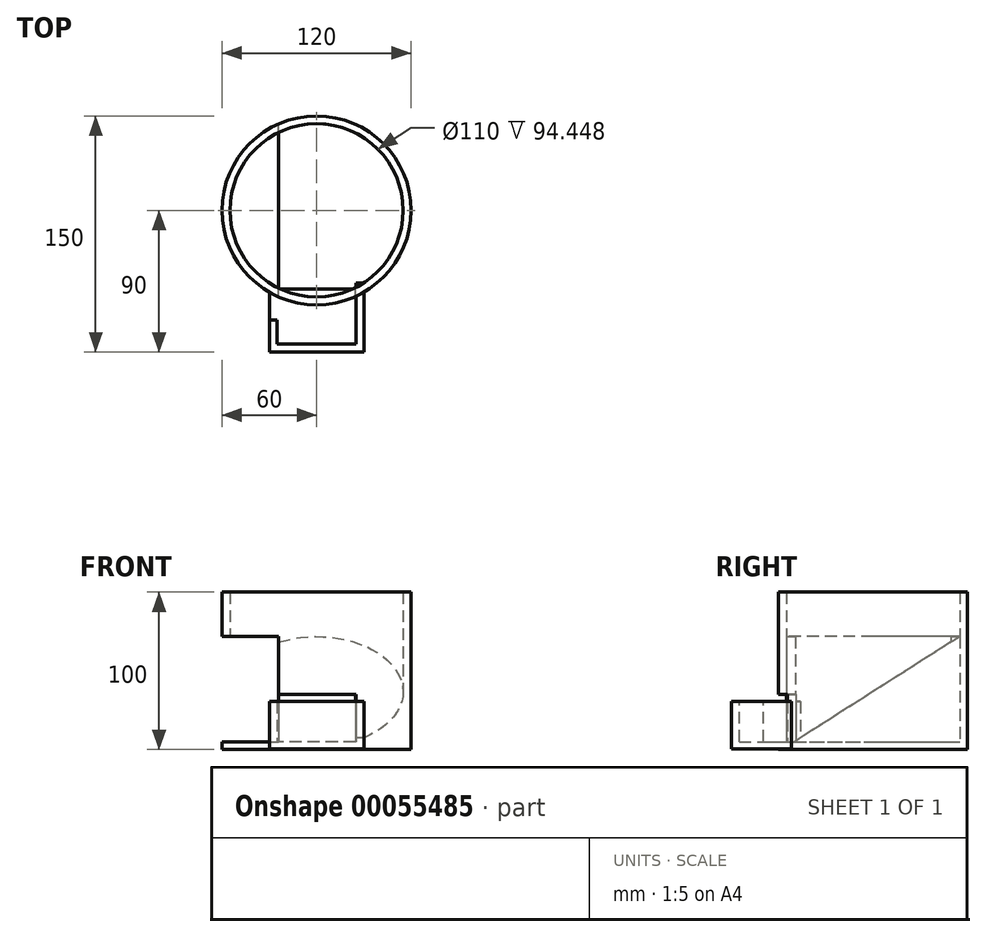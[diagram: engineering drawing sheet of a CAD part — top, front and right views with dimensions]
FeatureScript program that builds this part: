
annotation { "Feature Type Name" : "Feature", "Feature Type Description" : "" }
export const myFeature = defineFeature(function(context is Context, id is Id, definition is map)
    precondition{}
    {
        {
            var Q0;
            Q0=qCreatedBy(makeId("Front.planeOp"),FACE);
            var sketch = newSketch(context, id + "F0", { "sketchPlane" : qUnion([Q0])});
            skLineSegment(sketch, "E0", {"start": v(0, 0) * mm, "end": v(-55, 0) * mm});
            skLineSegment(sketch, "E1", {"start": v(-55, 0) * mm, "end": v(-55, 95) * mm});
            skLineSegment(sketch, "E2", {"start": v(-55, 95) * mm, "end": v(-60, 95) * mm});
            skLineSegment(sketch, "E3", {"start": v(-60, 95) * mm, "end": v(-60, -5) * mm});
            skLineSegment(sketch, "E4", {"start": v(-60, -5) * mm, "end": v(0, -5) * mm});
            skLineSegment(sketch, "E5", {"start": v(0, -5) * mm, "end": v(0, 0) * mm});
            skSolve(sketch);
        }
        {
            var Q0;
            Q0=makeQuery(id+"F0.imprint","IMPRINT",FACE,{"disambiguationData":[TD([[makeQuery(id+"F0.imprint","IMPRINT",EDGE,{"derivedFrom":sQuery(id+"F0.wireOp",EDGE,"E0")}),1.0]])]});
            var Q1;
            Q1=sQuery(id+"F0.wireOp",EDGE,"E5");
            revolve(context, id + "F1", {"entities" : qUnion([Q0]), "axis" : qUnion([Q1]), "revolveType" : RevolveType.FULL});
        }
        {
            var Q0;
            Q0=qCreatedBy(makeId("Front.planeOp"),FACE);
            var sketch = newSketch(context, id + "F2", { "sketchPlane" : qUnion([Q0])});
            skLineSegment(sketch, "E6", {"start": v(0, 0) * mm, "end": v(-26.4, 0) * mm});
            skLineSegment(sketch, "E7", {"start": v(-26.4, 0) * mm, "end": v(-26.4, 30) * mm});
            skLineSegment(sketch, "E8", {"start": v(-26.4, 30) * mm, "end": v(23.6, 30) * mm});
            skLineSegment(sketch, "E9", {"start": v(23.6, 30) * mm, "end": v(23.6, 0) * mm});
            skLineSegment(sketch, "E10", {"start": v(23.6, 0) * mm, "end": v(0, 0) * mm});
            skSolve(sketch);
        }
        {
            var Q0;
            Q0 = qSketchRegion(id + "F2", true);
            extrude(context, id + "F3", {"entities" : qUnion([Q0]), "operationType" : NewBodyOperationType.REMOVE, "depth" : 90 * mm});
        }
        {
            var Q0;
            Q0=qCreatedBy(makeId("Right.planeOp"),FACE);
            var sketch = newSketch(context, id + "F4", { "sketchPlane" : qUnion([Q0])});
            skLineSegment(sketch, "E11", {"start": v(0, 0) * mm, "end": v(0, -4.5) * mm});
            skLineSegment(sketch, "E12", {"start": v(0, -4.5) * mm, "end": v(-90, -4.5) * mm});
            skLineSegment(sketch, "E13", {"start": v(-90, -4.5) * mm, "end": v(-90, 25.5) * mm});
            skLineSegment(sketch, "E14", {"start": v(-90, 25.5) * mm, "end": v(-85, 25.5) * mm});
            skLineSegment(sketch, "E15", {"start": v(-85, 25.5) * mm, "end": v(-85, 0) * mm});
            skLineSegment(sketch, "E16", {"start": v(-85, 0) * mm, "end": v(0, 0) * mm});
            skSolve(sketch);
        }
        {
            var Q0;
            Q0=makeQuery(id+"F4.imprint","IMPRINT",FACE,{"disambiguationData":[TD([[makeQuery(id+"F4.imprint","IMPRINT",EDGE,{"derivedFrom":sQuery(id+"F4.wireOp",EDGE,"E11")}),-1.0]])]});
            extrude(context, id + "F5", {"entities" : qUnion([Q0]), "operationType" : NewBodyOperationType.ADD, "depth" : 25 * mm});
        }
        {
            var Q0;
            Q0=makeQuery(id+"F5.opExtrude","CAP_FACE",FACE,{"disambiguationData":[OSD([sQuery(id+"F4.wireOp",EDGE,"E11"),sQuery(id+"F4.wireOp",EDGE,"E12"),sQuery(id+"F4.wireOp",EDGE,"E13"),sQuery(id+"F4.wireOp",EDGE,"E14"),sQuery(id+"F4.wireOp",EDGE,"E15"),sQuery(id+"F4.wireOp",EDGE,"E16")])],"isStart":true});
            extrude(context, id + "F6", {"entities" : qUnion([Q0]), "operationType" : NewBodyOperationType.ADD, "depth" : 25 * mm});
        }
        {
            var Q0;
            Q0=makeQuery(id+"F5.opExtrude","CAP_FACE",FACE,{"disambiguationData":[OSD([sQuery(id+"F4.wireOp",EDGE,"E11"),sQuery(id+"F4.wireOp",EDGE,"E12"),sQuery(id+"F4.wireOp",EDGE,"E13"),sQuery(id+"F4.wireOp",EDGE,"E14"),sQuery(id+"F4.wireOp",EDGE,"E15"),sQuery(id+"F4.wireOp",EDGE,"E16")])],"isStart":false});
            var sketch = newSketch(context, id + "F7", { "sketchPlane" : qUnion([Q0])});
            skLineSegment(sketch, "E17", {"start": v(-90, 25.5) * mm, "end": v(-85, 25.5) * mm});
            skLineSegment(sketch, "E18", {"start": v(-85, 25.5) * mm, "end": v(-85, -4.5) * mm});
            skLineSegment(sketch, "E19", {"start": v(-85, -4.5) * mm, "end": v(-90, -4.5) * mm});
            skLineSegment(sketch, "E20", {"start": v(-90, -4.5) * mm, "end": v(-90, 25.5) * mm});
            skSolve(sketch);
        }
        {
            var Q0;
            {var subQ2=sQuery(id+"F7.wireOp",EDGE,"E17");Q0=makeQuery(id+"F7.imprint","IMPRINT",FACE,{"disambiguationData":[TD([[makeQuery(id+"F7.imprint","IMPRINT",EDGE,{"derivedFrom":subQ2}),-1.0]])]});}
            extrude(context, id + "F8", {"entities" : qUnion([Q0]), "operationType" : NewBodyOperationType.ADD, "depth" : 5 * mm});
        }
        {
            var Q0;
            Q0=makeQuery(id+"F6.opExtrude","CAP_FACE",FACE,{"disambiguationData":[OSD([sQuery(id+"F4.wireOp",EDGE,"E11"),sQuery(id+"F4.wireOp",EDGE,"E12"),sQuery(id+"F4.wireOp",EDGE,"E13"),sQuery(id+"F4.wireOp",EDGE,"E14"),sQuery(id+"F4.wireOp",EDGE,"E15"),sQuery(id+"F4.wireOp",EDGE,"E16")])],"isStart":false});
            var sketch = newSketch(context, id + "F9", { "sketchPlane" : qUnion([Q0])});
            skLineSegment(sketch, "E21", {"start": v(85, 0) * mm, "end": v(85, -4.5) * mm});
            skLineSegment(sketch, "E22", {"start": v(85, -4.5) * mm, "end": v(90, -4.5) * mm});
            skLineSegment(sketch, "E23", {"start": v(90, -4.5) * mm, "end": v(90, 25.5) * mm});
            skLineSegment(sketch, "E24", {"start": v(90, 25.5) * mm, "end": v(85, 25.5) * mm});
            skLineSegment(sketch, "E25", {"start": v(85, 25.5) * mm, "end": v(85, 0) * mm});
            skSolve(sketch);
        }
        {
            var Q0;
            Q0=makeQuery(id+"F9.imprint","IMPRINT",FACE,{"disambiguationData":[TD([[makeQuery(id+"F9.imprint","IMPRINT",EDGE,{"derivedFrom":sQuery(id+"F9.wireOp",EDGE,"E21")}),1.0]])]});
            extrude(context, id + "F10", {"entities" : qUnion([Q0]), "operationType" : NewBodyOperationType.ADD, "depth" : 5 * mm});
        }
        {
            var Q0;
            Q0=makeQuery(id+"F6.opExtrude","SWEPT_FACE",FACE,{"disambiguationData":[OSD([sQuery(id+"F0.wireOp",EDGE,"E3"),sQuery(id+"F4.wireOp",EDGE,"E11"),sQuery(id+"F4.wireOp",EDGE,"E12"),sQuery(id+"F4.wireOp",EDGE,"E13"),sQuery(id+"F4.wireOp",EDGE,"E14"),sQuery(id+"F4.wireOp",EDGE,"E15"),sQuery(id+"F4.wireOp",EDGE,"E16")])]});
            extrude(context, id + "F11", {"entities" : qUnion([Q0]), "operationType" : NewBodyOperationType.ADD, "depth" : 31.41 * mm});
        }
        {
            var Q0;
            {var subQ0=sQuery(id+"F4.wireOp",EDGE,"E15");Q0=makeQuery(id+"F10.boolean.opBoolean","MERGE",FACE,{"derivedFrom":[makeQuery(id+"F8.boolean.opBoolean","MERGE",FACE,{"derivedFrom":[makeQuery(id+"F6.boolean.opBoolean","MERGE",FACE,{"derivedFrom":[makeQuery(id+"F5.opExtrude","SWEPT_FACE",FACE,{"disambiguationData":[OSD([subQ0])]}),makeQuery(id+"F6.opExtrude","SWEPT_FACE",FACE,{"disambiguationData":[OSD([subQ0])]})]}),makeQuery(id+"F8.opExtrude","SWEPT_FACE",FACE,{"disambiguationData":[OSD([sQuery(id+"F7.wireOp",EDGE,"E18")])]})]}),makeQuery(id+"F10.opExtrude","SWEPT_FACE",FACE,{"disambiguationData":[OSD([sQuery(id+"F9.wireOp",EDGE,"E21"),sQuery(id+"F9.wireOp",EDGE,"E25")])]})]});}
            var sketch = newSketch(context, id + "F12", { "sketchPlane" : qUnion([Q0])});
            skLineSegment(sketch, "E26", {"start": v(30, 10.5) * mm, "end": v(30, 25.5) * mm});
            skLineSegment(sketch, "E27", {"start": v(30, 25.5) * mm, "end": v(30, -4.5) * mm});
            skLineSegment(sketch, "E28", {"start": v(30, -4.5) * mm, "end": v(25, -4.5) * mm});
            skLineSegment(sketch, "E29", {"start": v(25, -4.5) * mm, "end": v(25, 0) * mm});
            skLineSegment(sketch, "E30", {"start": v(25, 0) * mm, "end": v(25, 25.5) * mm});
            skLineSegment(sketch, "E31", {"start": v(25, 25.5) * mm, "end": v(30, 25.5) * mm});
            skSolve(sketch);
        }
        {
            var Q0;
            {var subQ1=sQuery(id+"F12.wireOp",EDGE,"E28");Q0=makeQuery(id+"F12.imprint","IMPRINT",FACE,{"disambiguationData":[TD([[makeQuery(id+"F12.imprint","IMPRINT",EDGE,{"derivedFrom":subQ1}),-1.0]])]});}
            extrude(context, id + "F13", {"entities" : qUnion([Q0]), "operationType" : NewBodyOperationType.ADD, "depth" : 52.46 * mm});
        }
        {
            var Q0;
            {var subQ0=sQuery(id+"F4.wireOp",EDGE,"E15");Q0=makeQuery(id+"F10.boolean.opBoolean","MERGE",FACE,{"derivedFrom":[makeQuery(id+"F8.boolean.opBoolean","MERGE",FACE,{"derivedFrom":[makeQuery(id+"F6.boolean.opBoolean","MERGE",FACE,{"derivedFrom":[makeQuery(id+"F5.opExtrude","SWEPT_FACE",FACE,{"disambiguationData":[OSD([subQ0])]}),makeQuery(id+"F6.opExtrude","SWEPT_FACE",FACE,{"disambiguationData":[OSD([subQ0])]})]}),makeQuery(id+"F8.opExtrude","SWEPT_FACE",FACE,{"disambiguationData":[OSD([sQuery(id+"F7.wireOp",EDGE,"E18")])]})]}),makeQuery(id+"F10.opExtrude","SWEPT_FACE",FACE,{"disambiguationData":[OSD([sQuery(id+"F9.wireOp",EDGE,"E21"),sQuery(id+"F9.wireOp",EDGE,"E25")])]})]});}
            var sketch = newSketch(context, id + "F14", { "sketchPlane" : qUnion([Q0])});
            skLineSegment(sketch, "E32", {"start": v(-30, 25.5) * mm, "end": v(-30, -4.5) * mm});
            skLineSegment(sketch, "E33", {"start": v(-30, -4.5) * mm, "end": v(-25, -4.5) * mm});
            skLineSegment(sketch, "E34", {"start": v(-25, -4.5) * mm, "end": v(-25, 0) * mm});
            skLineSegment(sketch, "E35", {"start": v(-25, 0) * mm, "end": v(-25, 25.5) * mm});
            skLineSegment(sketch, "E36", {"start": v(-25, 25.5) * mm, "end": v(-30, 25.5) * mm});
            skSolve(sketch);
        }
        {
            var Q0;
            Q0=makeQuery(id+"F14.imprint","IMPRINT",FACE,{"disambiguationData":[TD([[makeQuery(id+"F14.imprint","IMPRINT",EDGE,{"derivedFrom":sQuery(id+"F14.wireOp",EDGE,"E32")}),1.0]])]});
            extrude(context, id + "F15", {"entities" : qUnion([Q0]), "operationType" : NewBodyOperationType.ADD, "depth" : 44.88 * mm});
        }
        {
            var Q0;
            Q0=makeQuery(id+"F13.opExtrude","CAP_FACE",FACE,{"disambiguationData":[OSD([sQuery(id+"F12.wireOp",EDGE,"E27"),sQuery(id+"F12.wireOp",EDGE,"E28"),sQuery(id+"F12.wireOp",EDGE,"E29"),sQuery(id+"F12.wireOp",EDGE,"E30"),sQuery(id+"F12.wireOp",EDGE,"E31")])],"isStart":false});
            extrude(context, id + "F16", {"entities" : qUnion([Q0]), "operationType" : NewBodyOperationType.REMOVE, "oppositeDirection" : true, "depth" : 13.6 * mm});
        }
        {
            var Q0;
            Q0=makeQuery(id+"F15.opExtrude","CAP_FACE",FACE,{"disambiguationData":[OSD([sQuery(id+"F14.wireOp",EDGE,"E32"),sQuery(id+"F14.wireOp",EDGE,"E33"),sQuery(id+"F14.wireOp",EDGE,"E34"),sQuery(id+"F14.wireOp",EDGE,"E35"),sQuery(id+"F14.wireOp",EDGE,"E36")])],"isStart":false});
            extrude(context, id + "F17", {"entities" : qUnion([Q0]), "operationType" : NewBodyOperationType.REMOVE, "oppositeDirection" : true, "depth" : 6.08 * mm});
        }
        {
            var Q0;
            Q0=makeQuery(id+"F3.boolean.opBoolean","COPY",FACE,{"derivedFrom":makeQuery(id+"F3.opExtrude","SWEPT_FACE",FACE,{"disambiguationData":[OSD([sQuery(id+"F2.wireOp",EDGE,"E9")])]})});
            extrude(context, id + "F18", {"entities" : qUnion([Q0]), "operationType" : NewBodyOperationType.ADD, "oppositeDirection" : true, "depth" : 1.34 * mm});
        }
        {
            var Q0;
            Q0=makeQuery(id+"F3.boolean.opBoolean","COPY",FACE,{"derivedFrom":makeQuery(id+"F3.opExtrude","SWEPT_FACE",FACE,{"disambiguationData":[OSD([sQuery(id+"F2.wireOp",EDGE,"E9")])]})});
            extrude(context, id + "F19", {"entities" : qUnion([Q0]), "operationType" : NewBodyOperationType.REMOVE, "oppositeDirection" : true, "depth" : 1.1 * mm});
        }
        {
            var Q0;
            Q0=makeQuery(id+"F19.boolean.opBoolean","COPY",FACE,{"derivedFrom":makeQuery(id+"F19.opExtrude","SWEPT_FACE",FACE,{"disambiguationData":[OSD([sQuery(id+"F0.wireOp",EDGE,"E1"),sQuery(id+"F2.wireOp",EDGE,"E9")])]})});
            extrude(context, id + "F20", {"entities" : qUnion([Q0]), "operationType" : NewBodyOperationType.REMOVE, "oppositeDirection" : true, "depth" : 47.9 * mm});
        }
        {
            var Q0;
            Q0=makeQuery(id+"F3.boolean.opBoolean","COPY",FACE,{"derivedFrom":makeQuery(id+"F3.opExtrude","SWEPT_FACE",FACE,{"disambiguationData":[OSD([sQuery(id+"F2.wireOp",EDGE,"E7")])]})});
            extrude(context, id + "F21", {"entities" : qUnion([Q0]), "operationType" : NewBodyOperationType.ADD, "depth" : 1.15 * mm});
        }
        {
            var Q0;
            Q0=qCreatedBy(makeId("Right.planeOp"),FACE);
            var sketch = newSketch(context, id + "F22", { "sketchPlane" : qUnion([Q0])});
            skLineSegment(sketch, "E37", {"start": v(0, 0) * mm, "end": v(60, 0) * mm});
            skLineSegment(sketch, "E38", {"start": v(60, 0) * mm, "end": v(60, 70) * mm});
            skLineSegment(sketch, "E39", {"start": v(60, 70) * mm, "end": v(-50, 0) * mm});
            skLineSegment(sketch, "E40", {"start": v(-50, 0) * mm, "end": v(0, 0) * mm});
            skSolve(sketch);
        }
        {
            var Q0;
            Q0=makeQuery(id+"F22.imprint","IMPRINT",FACE,{"disambiguationData":[TD([[makeQuery(id+"F22.imprint","IMPRINT",EDGE,{"derivedFrom":sQuery(id+"F22.wireOp",EDGE,"E37")}),1.0]])]});
            extrude(context, id + "F23", {"entities" : qUnion([Q0]), "operationType" : NewBodyOperationType.ADD, "depth" : 60.8 * mm});
        }
        {
            var Q0;
            Q0=makeQuery(id+"F23.opExtrude","SWEPT_FACE",FACE,{"disambiguationData":[OSD([sQuery(id+"F22.wireOp",EDGE,"E37"),sQuery(id+"F22.wireOp",EDGE,"E40")])]});
            extrude(context, id + "F24", {"entities" : qUnion([Q0]), "operationType" : NewBodyOperationType.REMOVE, "oppositeDirection" : true, "depth" : 160.23 * mm});
        }
        {
            var Q0;
            Q0=makeQuery(id+"F23.opExtrude","CAP_FACE",FACE,{"disambiguationData":[OSD([sQuery(id+"F22.wireOp",EDGE,"E37"),sQuery(id+"F22.wireOp",EDGE,"E38"),sQuery(id+"F22.wireOp",EDGE,"E39"),sQuery(id+"F22.wireOp",EDGE,"E40")])],"isStart":true});
            extrude(context, id + "F25", {"entities" : qUnion([Q0]), "operationType" : NewBodyOperationType.ADD, "depth" : 98.94 * mm});
        }
        {
            var Q0;
            Q0=makeQuery(id+"F25.opExtrude","SWEPT_FACE",FACE,{"disambiguationData":[OSD([sQuery(id+"F22.wireOp",EDGE,"E37"),sQuery(id+"F22.wireOp",EDGE,"E40")])]});
            extrude(context, id + "F26", {"entities" : qUnion([Q0]), "operationType" : NewBodyOperationType.REMOVE, "oppositeDirection" : true, "depth" : 124.74 * mm});
        }
    });
